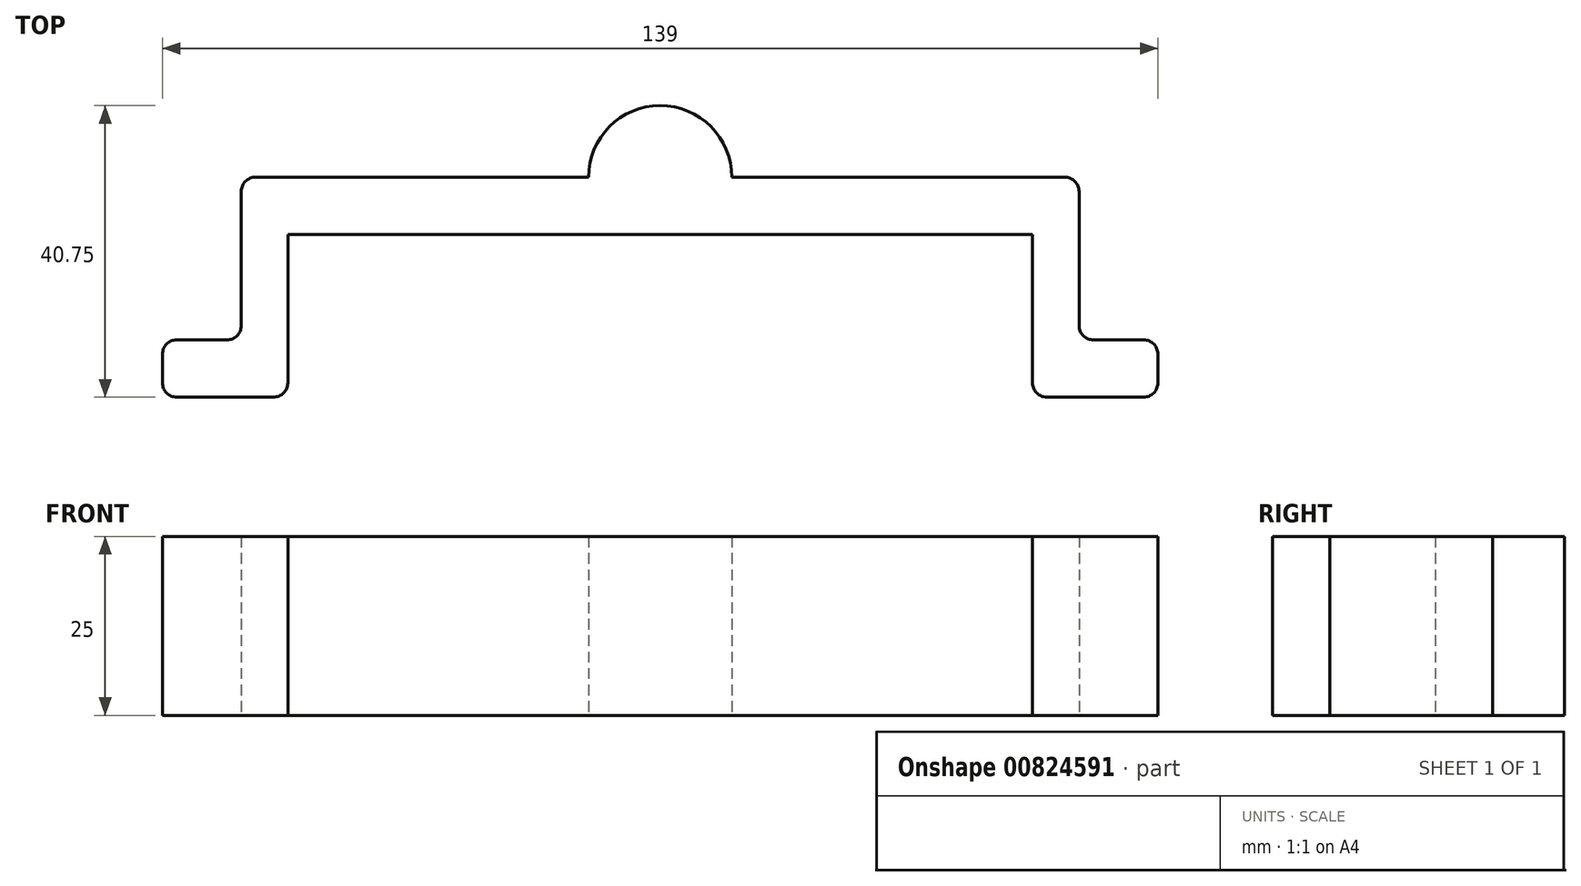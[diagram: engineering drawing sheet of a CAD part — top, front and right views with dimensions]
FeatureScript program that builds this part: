
annotation { "Feature Type Name" : "Feature", "Feature Type Description" : "" }
export const myFeature = defineFeature(function(context is Context, id is Id, definition is map)
    precondition{}
    {
        {
            var Q0;
            Q0=qCreatedBy(makeId("Top.planeOp"),FACE);
            var sketch = newSketch(context, id + "F0", { "sketchPlane" : qUnion([Q0])});
            skLineSegment(sketch, "E0", {"start": v(0, 0) * mm, "end": v(-42, 0) * mm});
            skLineSegment(sketch, "E1", {"start": v(-42, 0) * mm, "end": v(-42, -20.75) * mm});
            skLineSegment(sketch, "E2", {"start": v(-44, -22.75) * mm, "end": v(-57.5, -22.75) * mm});
            skLineSegment(sketch, "E3", {"start": v(-59.5, -20.75) * mm, "end": v(-59.5, -16.75) * mm});
            skLineSegment(sketch, "E4", {"start": v(-57.5, -14.75) * mm, "end": v(-50.5, -14.75) * mm});
            skLineSegment(sketch, "E5", {"start": v(-48.5, -12.75) * mm, "end": v(-48.5, 6) * mm});
            skLineSegment(sketch, "E6", {"start": v(-46.5, 8) * mm, "end": v(0, 8) * mm});
            skLineSegment(sketch, "E7", {"start": v(20, 8) * mm, "end": v(0, 8) * mm});
            skLineSegment(sketch, "E8", {"start": v(0, 0) * mm, "end": v(10, 0) * mm});
            skLineSegment(sketch, "E9", {"start": v(10, 0) * mm, "end": v(10, -13.02) * mm, "construction": true});
            skLineSegment(sketch, "E10.MirrorCS", {"start": v(20, 0) * mm, "end": v(10, 0) * mm});
            skLineSegment(sketch, "E11.MirrorCS", {"start": v(66.5, 8) * mm, "end": v(20, 8) * mm});
            skLineSegment(sketch, "E12.MirrorCS", {"start": v(68.5, -12.75) * mm, "end": v(68.5, 6) * mm});
            skLineSegment(sketch, "E13.MirrorCS", {"start": v(77.5, -14.75) * mm, "end": v(70.5, -14.75) * mm});
            skLineSegment(sketch, "E14.MirrorCS", {"start": v(79.5, -20.75) * mm, "end": v(79.5, -16.75) * mm});
            skLineSegment(sketch, "E15.MirrorCS", {"start": v(64, -22.75) * mm, "end": v(77.5, -22.75) * mm});
            skLineSegment(sketch, "E16.MirrorCS", {"start": v(62, 0) * mm, "end": v(62, -20.75) * mm});
            skLineSegment(sketch, "E17.MirrorCS", {"start": v(20, 0) * mm, "end": v(62, 0) * mm});
            skPoint(sketch, "E18.visualSharp", {"position": v(-42, -22.75) * mm});
            skArc(sketch, "E18.filletArc", {"start": v(-44, -22.75) * mm, "mid": v(-42.59, -22.16) * mm, "end": v(-42, -20.75) * mm});
            skPoint(sketch, "E19.visualSharp", {"position": v(62, -22.75) * mm});
            skArc(sketch, "E19.filletArc", {"start": v(62, -20.75) * mm, "mid": v(62.59, -22.16) * mm, "end": v(64, -22.75) * mm});
            skArc(sketch, "E20.filletArc", {"start": v(-46.5, 8) * mm, "mid": v(-47.91, 7.41) * mm, "end": v(-48.5, 6) * mm});
            skArc(sketch, "E21.filletArc", {"start": v(68.5, 6) * mm, "mid": v(67.91, 7.41) * mm, "end": v(66.5, 8) * mm});
            skPoint(sketch, "E22.visualSharp", {"position": v(71.5, 246.8) * mm});
            skArc(sketch, "E22.filletArc", {"start": v(71.5, 228.04) * mm, "mid": v(69.71, 230.03) * mm, "end": v(67.54, 228.46) * mm});
            skPoint(sketch, "E23.visualSharp", {"position": v(79.5, -22.75) * mm});
            skArc(sketch, "E23.filletArc", {"start": v(77.5, -22.75) * mm, "mid": v(78.91, -22.16) * mm, "end": v(79.5, -20.75) * mm});
            skPoint(sketch, "E24.visualSharp", {"position": v(-59.5, -22.75) * mm});
            skArc(sketch, "E24.filletArc", {"start": v(-59.5, -20.75) * mm, "mid": v(-58.91, -22.16) * mm, "end": v(-57.5, -22.75) * mm});
            skPoint(sketch, "E25.visualSharp", {"position": v(-59.5, -14.75) * mm});
            skArc(sketch, "E25.filletArc", {"start": v(-57.5, -14.75) * mm, "mid": v(-58.91, -15.34) * mm, "end": v(-59.5, -16.75) * mm});
            skPoint(sketch, "E26.visualSharp", {"position": v(79.5, -14.75) * mm});
            skArc(sketch, "E26.filletArc", {"start": v(79.5, -16.75) * mm, "mid": v(78.91, -15.34) * mm, "end": v(77.5, -14.75) * mm});
            skPoint(sketch, "E27.visualSharp", {"position": v(68.5, -14.75) * mm});
            skArc(sketch, "E27.filletArc", {"start": v(68.5, -12.75) * mm, "mid": v(69.09, -14.16) * mm, "end": v(70.5, -14.75) * mm});
            skPoint(sketch, "E28.visualSharp", {"position": v(-48.5, -14.75) * mm});
            skArc(sketch, "E28.filletArc", {"start": v(-50.5, -14.75) * mm, "mid": v(-49.09, -14.16) * mm, "end": v(-48.5, -12.75) * mm});
            skArc(sketch, "E29", {"start": v(20, 8) * mm, "mid": v(10, 18) * mm, "end": v(0, 8) * mm});
            skSolve(sketch);
        }
        {
            var Q0;
            Q0=makeQuery(id+"F0.imprint","IMPRINT",FACE,{"disambiguationData":[TD([[makeQuery(id+"F0.imprint","IMPRINT",EDGE,{"derivedFrom":sQuery(id+"F0.wireOp",EDGE,"E0")}),-1.0]])]});
            var Q1;
            Q1=makeQuery(id+"F0.imprint","IMPRINT",FACE,{"disambiguationData":[TD([[makeQuery(id+"F0.imprint","IMPRINT",EDGE,{"derivedFrom":sQuery(id+"F0.wireOp",EDGE,"E7")}),-1.0]])]});
            extrude(context, id + "F1", {"entities" : qUnion([Q0, Q1]), "depth" : 25 * mm, "offsetDistance" : 25 * mm});
        }
    });
